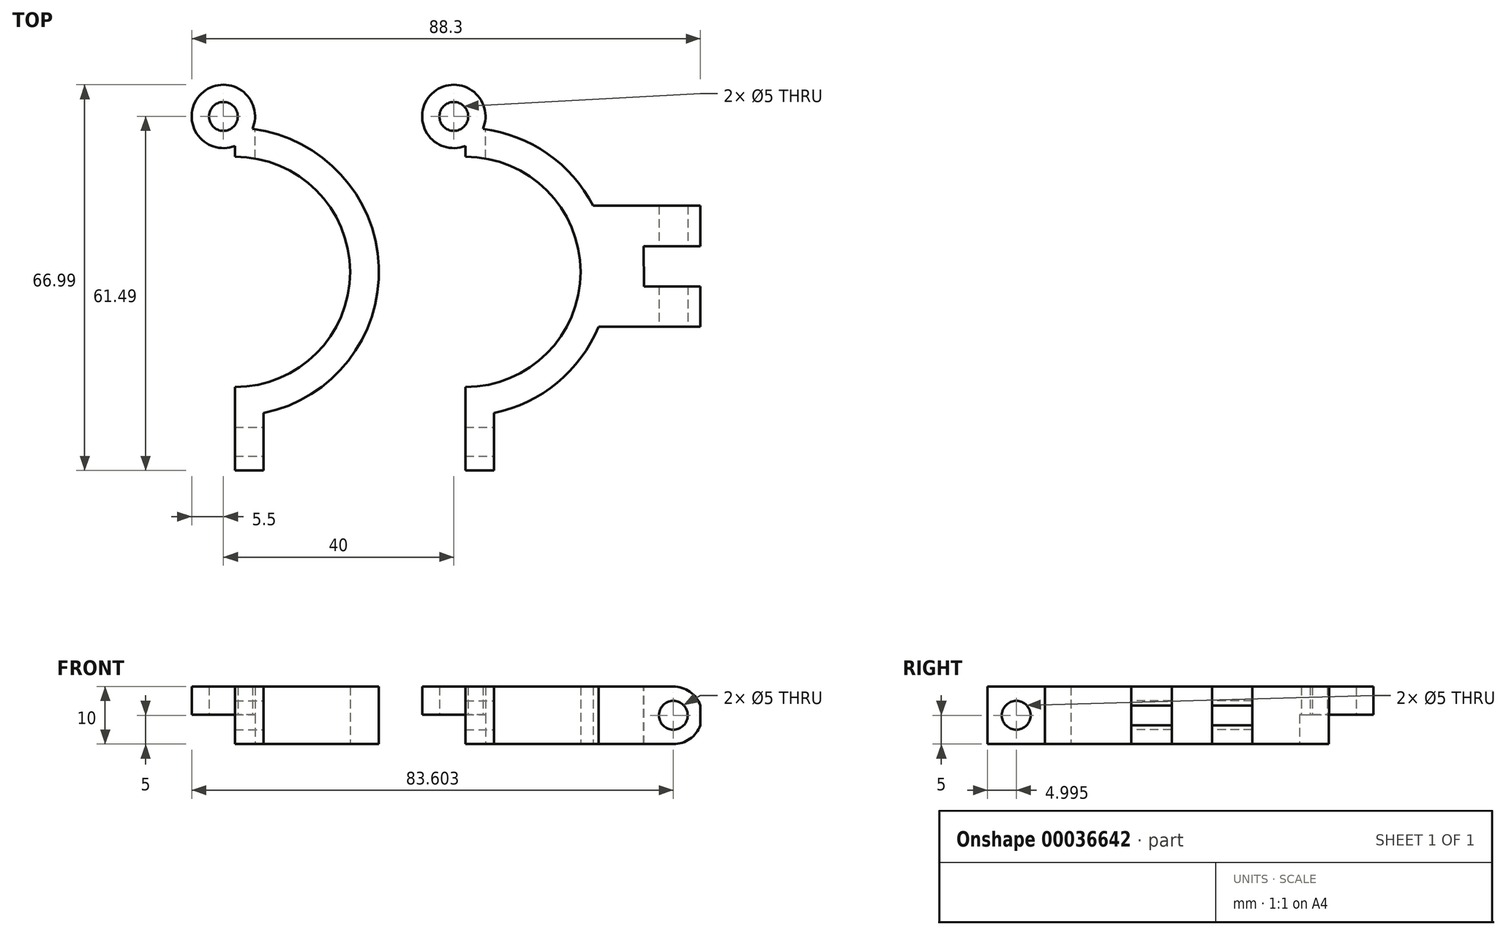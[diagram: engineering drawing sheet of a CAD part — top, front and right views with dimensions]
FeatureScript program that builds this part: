
annotation { "Feature Type Name" : "Feature", "Feature Type Description" : "" }
export const myFeature = defineFeature(function(context is Context, id is Id, definition is map)
    precondition{}
    {
        {
            var Q0;
            Q0=qCreatedBy(makeId("Top.planeOp"),FACE);
            var sketch = newSketch(context, id + "F0", { "sketchPlane" : qUnion([Q0])});
            skArc(sketch, "E0", {"start": v(0, -20) * mm, "mid": v(20, 0) * mm, "end": v(0, 20) * mm});
            skArc(sketch, "E1", {"start": v(5, -24.5) * mm, "mid": v(24.87, 2.51) * mm, "end": v(0, 25) * mm});
            skLineSegment(sketch, "E2", {"start": v(0, 25) * mm, "end": v(0, 20) * mm});
            skLineSegment(sketch, "E3.trimOffspring", {"start": v(0, -20) * mm, "end": v(0, -25) * mm});
            skLineSegment(sketch, "E4.top", {"start": v(0, -34.5) * mm, "end": v(5, -34.5) * mm});
            skLineSegment(sketch, "E4.left", {"start": v(0, -20) * mm, "end": v(0, -34.5) * mm});
            skLineSegment(sketch, "E4.right", {"start": v(5, -24.5) * mm, "end": v(5, -34.5) * mm});
            skLineSegment(sketch, "E5", {"start": v(0, 25) * mm, "end": v(-2, 25) * mm, "construction": true});
            skLineSegment(sketch, "E6", {"start": v(-2, 25) * mm, "end": v(-2, 27) * mm, "construction": true});
            skCircle(sketch, "E7", {"center": v(-2, 27) * mm, "radius": 2.5 * mm});
            skCircle(sketch, "E8", {"center": v(-2, 27) * mm, "radius": 5.5 * mm});
            skSolve(sketch);
        }
        {
            var Q0;
            Q0 = qSketchRegion(id + "F0", true);
            extrude(context, id + "F1", {"entities" : qUnion([Q0]), "depth" : 10 * mm});
        }
        {
            var Q0;
            Q0=makeQuery(id+"F1.opExtrude","CAP_FACE",FACE,{"disambiguationData":[OSD([sQuery(id+"F0.wireOp",EDGE,"E0"),sQuery(id+"F0.wireOp",EDGE,"E1"),sQuery(id+"F0.wireOp",EDGE,"E2"),sQuery(id+"F0.wireOp",EDGE,"E4.top"),sQuery(id+"F0.wireOp",EDGE,"E4.left"),sQuery(id+"F0.wireOp",EDGE,"E4.right"),sQuery(id+"F0.wireOp",EDGE,"40993b52-42f4-45ce-a234-201135d0f319"),sQuery(id+"F0.wireOp",EDGE,"b42522cb-95ce-463a-b71a-0f81370b394c")])],"isStart":true});
            var sketch = newSketch(context, id + "F2", { "sketchPlane" : qUnion([Q0])});
            skArc(sketch, "E9.0", {"start": v(3.5, -27) * mm, "mid": v(-6.54, -30.1) * mm, "end": v(0, -21.88) * mm});
            skLineSegment(sketch, "E10.bottom", {"start": v(0, -15.05) * mm, "end": v(3.5, -15.05) * mm});
            skLineSegment(sketch, "E10.left", {"start": v(0, -15.05) * mm, "end": v(0, -21.88) * mm});
            skLineSegment(sketch, "E10.right", {"start": v(3.5, -15.05) * mm, "end": v(3.5, -27) * mm});
            skSolve(sketch);
        }
        {
            var Q0;
            Q0 = qSketchRegion(id + "F2", true);
            extrude(context, id + "F3", {"entities" : qUnion([Q0]), "operationType" : NewBodyOperationType.REMOVE, "oppositeDirection" : true, "depth" : 5.1 * mm});
        }
        {
            var Q0;
            Q0=makeQuery(id+"F1.opExtrude","SWEPT_FACE",FACE,{"disambiguationData":[OSD([sQuery(id+"F0.wireOp",EDGE,"E4.right")])]});
            var sketch = newSketch(context, id + "F4", { "sketchPlane" : qUnion([Q0])});
            skLineSegment(sketch, "E11.0.0", {"start": v(-34.5, 0) * mm, "end": v(-24.5, 0) * mm, "construction": true});
            skLineSegment(sketch, "E11.0.1", {"start": v(-24.5, 0) * mm, "end": v(-24.5, 10) * mm, "construction": true});
            skLineSegment(sketch, "E11.0.2", {"start": v(-24.5, 10) * mm, "end": v(-34.5, 10) * mm, "construction": true});
            skLineSegment(sketch, "E11.0.3", {"start": v(-34.5, 10) * mm, "end": v(-34.5, 0) * mm, "construction": true});
            skCircle(sketch, "E12", {"center": v(-29.5, 5) * mm, "radius": 2.5 * mm});
            skPoint(sketch, "E12.centerSnap0", {"position": v(-29.5, 10) * mm});
            skPoint(sketch, "E12.centerSnap1", {"position": v(-34.5, 5) * mm});
            skSolve(sketch);
        }
        {
            var Q0;
            Q0 = qSketchRegion(id + "F4", true);
            extrude(context, id + "F5", {"entities" : qUnion([Q0]), "operationType" : NewBodyOperationType.REMOVE, "oppositeDirection" : true, "depth" : 25 * mm});
        }
        {
            var Q0;
            Q0=makeQuery(id+"F1.opExtrude","SWEPT_BODY",BODY,{"disambiguationData":[OSD([sQuery(id+"F0.wireOp",EDGE,"E0"),sQuery(id+"F0.wireOp",EDGE,"E1"),sQuery(id+"F0.wireOp",EDGE,"E2"),sQuery(id+"F0.wireOp",EDGE,"E4.top"),sQuery(id+"F0.wireOp",EDGE,"E4.left"),sQuery(id+"F0.wireOp",EDGE,"E4.right"),sQuery(id+"F0.wireOp",EDGE,"E7"),sQuery(id+"F0.wireOp",EDGE,"E8")])]});
            transform(context, id + "F6", {"entities" : qUnion([Q0]), "transformType" : TransformType.TRANSLATION_3D, "dx" : 40 * mm, "dy" : 0 * mm, "dz" : 0 * mm, "makeCopy" : true});
        }
        {
            var Q0;
            Q0=makeQuery(id+"F6.opPattern","COPY",FACE,{"derivedFrom":makeQuery(id+"F1.opExtrude","CAP_FACE",FACE,{"disambiguationData":[OSD([sQuery(id+"F0.wireOp",EDGE,"E0"),sQuery(id+"F0.wireOp",EDGE,"E1"),sQuery(id+"F0.wireOp",EDGE,"E2"),sQuery(id+"F0.wireOp",EDGE,"E4.top"),sQuery(id+"F0.wireOp",EDGE,"E4.left"),sQuery(id+"F0.wireOp",EDGE,"E4.right"),sQuery(id+"F0.wireOp",EDGE,"E7"),sQuery(id+"F0.wireOp",EDGE,"E8")])],"isStart":false}),"instanceName":"1"});
            var sketch = newSketch(context, id + "F7", { "sketchPlane" : qUnion([Q0])});
            skLineSegment(sketch, "E13.rect.bottom", {"start": v(61.08, -9.51) * mm, "end": v(81.1, -9.51) * mm});
            skLineSegment(sketch, "E13.rect.top", {"start": v(60.88, 11.49) * mm, "end": v(80.89, 11.49) * mm});
            skPoint(sketch, "E13.rect.middle", {"position": v(64.98, 0.99) * mm});
            skLineSegment(sketch, "E14.0", {"start": v(61.08, -9.51) * mm, "end": v(60.88, 11.49) * mm});
            skLineSegment(sketch, "E15.0", {"start": v(60.88, 4.49) * mm, "end": v(60.95, 4.49) * mm});
            skLineSegment(sketch, "E16.0", {"start": v(60.88, -2.51) * mm, "end": v(61.01, -2.51) * mm});
            skLineSegment(sketch, "E17.0", {"start": v(71.08, -9.6) * mm, "end": v(71.08, -9.51) * mm});
            skLineSegment(sketch, "E18.trimOffspring", {"start": v(70.95, 4.49) * mm, "end": v(80.89, 4.49) * mm});
            skLineSegment(sketch, "E19.trimOffspring", {"start": v(71.01, -2.51) * mm, "end": v(81.01, -2.51) * mm});
            skLineSegment(sketch, "E20.trimOffspring", {"start": v(71.01, -2.51) * mm, "end": v(70.95, 4.49) * mm});
            skLineSegment(sketch, "E21", {"start": v(80.89, 11.49) * mm, "end": v(80.89, 4.49) * mm});
            skLineSegment(sketch, "E22", {"start": v(81.01, -2.51) * mm, "end": v(81.1, -9.51) * mm});
            skSolve(sketch);
        }
        {
            var Q0;
            Q0 = qSketchRegion(id + "F7", true);
            extrude(context, id + "F8", {"entities" : qUnion([Q0]), "operationType" : NewBodyOperationType.ADD, "oppositeDirection" : true, "depth" : 10 * mm});
        }
        {
            var Q0;
            Q0=makeQuery(id+"F8.opExtrude","SWEPT_FACE",FACE,{"disambiguationData":[OSD([sQuery(id+"F7.wireOp",EDGE,"E13.rect.bottom")])]});
            var sketch = newSketch(context, id + "F9", { "sketchPlane" : qUnion([Q0])});
            skLineSegment(sketch, "E23.0", {"start": v(71.1, 0) * mm, "end": v(71.1, 10) * mm});
            skLineSegment(sketch, "E24.0.1", {"start": v(71.1, 0) * mm, "end": v(81.1, 0) * mm});
            skLineSegment(sketch, "E24.0.2", {"start": v(81.1, 0) * mm, "end": v(81.1, 10) * mm});
            skLineSegment(sketch, "E24.0.3", {"start": v(81.1, 10) * mm, "end": v(71.1, 10) * mm});
            skCircle(sketch, "E25", {"center": v(76.1, 5) * mm, "radius": 2.5 * mm});
            skPoint(sketch, "E25.centerSnap0", {"position": v(81.1, 5) * mm});
            skPoint(sketch, "E25.centerSnap1", {"position": v(76.1, 10) * mm});
            skSolve(sketch);
        }
        {
            var Q0;
            Q0=makeQuery(id+"F9.imprint","IMPRINT",FACE,{"disambiguationData":[TD([[makeQuery(id+"F9.imprint","IMPRINT",EDGE,{"derivedFrom":sQuery(id+"F9.wireOp",EDGE,"E25")}),1.0]])]});
            extrude(context, id + "F10", {"entities" : qUnion([Q0]), "operationType" : NewBodyOperationType.REMOVE, "oppositeDirection" : true, "depth" : 25 * mm});
        }
        {
            var Q0;
            Q0=makeQuery(id+"F8.opExtrude","SWEPT_FACE",FACE,{"disambiguationData":[OSD([sQuery(id+"F7.wireOp",EDGE,"E13.rect.bottom")])]});
            var sketch = newSketch(context, id + "F11", { "sketchPlane" : qUnion([Q0])});
            skArc(sketch, "E26", {"start": v(76.1, 0) * mm, "mid": v(81.1, 5) * mm, "end": v(76.1, 10) * mm});
            skLineSegment(sketch, "E27.bottom", {"start": v(81.1, 10) * mm, "end": v(76.1, 10) * mm});
            skLineSegment(sketch, "E27.top", {"start": v(80.98, 0) * mm, "end": v(76.1, 0) * mm});
            skLineSegment(sketch, "E28.0", {"start": v(80.8, 0) * mm, "end": v(80.8, 10) * mm});
            skSolve(sketch);
        }
        {
            var Q0;
            {var subQ3=sQuery(id+"F11.wireOp",EDGE,"E27.bottom");Q0=makeQuery(id+"F11.imprint","IMPRINT",FACE,{"disambiguationData":[TD([[makeQuery(id+"F11.imprint","IMPRINT",EDGE,{"derivedFrom":subQ3}),-1.0]])]});}
            var Q1;
            {var subQ3=sQuery(id+"F11.wireOp",EDGE,"E27.top");Q1=makeQuery(id+"F11.imprint","IMPRINT",FACE,{"disambiguationData":[TD([[makeQuery(id+"F11.imprint","IMPRINT",EDGE,{"derivedFrom":subQ3}),1.0]])]});}
            var Q2;
            {var subQ3=sQuery(id+"F11.wireOp",EDGE,"E27.top");var subQ5=sQuery(id+"F11.wireOp",EDGE,"E28.0");var subQ7=makeQuery(id+"F11.imprint","INTERSECT",VERTEX,{"derivedFrom":[subQ3,subQ5]});Q2=makeQuery(id+"F11.imprint","IMPRINT",FACE,{"disambiguationData":[TD([[makeQuery(id+"F11.imprint","IMPRINT",EDGE,{"disambiguationData":[TD([[subQ7,-1.0]])],"derivedFrom":subQ5}),-1.0]])]});}
            var Q3;
            {var subQ3=sQuery(id+"F11.wireOp",EDGE,"E27.bottom");var subQ5=sQuery(id+"F11.wireOp",EDGE,"E28.0");var subQ7=makeQuery(id+"F11.imprint","INTERSECT",VERTEX,{"derivedFrom":[subQ3,subQ5]});Q3=makeQuery(id+"F11.imprint","IMPRINT",FACE,{"disambiguationData":[TD([[makeQuery(id+"F11.imprint","IMPRINT",EDGE,{"disambiguationData":[TD([[subQ7,1.0]])],"derivedFrom":subQ5}),-1.0]])]});}
            var Q4;
            {var subQ0=sQuery(id+"F11.wireOp",EDGE,"E28.0");var subQ1=sQuery(id+"F11.wireOp",EDGE,"E26");var subQ3=makeQuery(id+"F11.imprint","INTERSECT",VERTEX,{"disambiguationData":[OD(0.0)],"derivedFrom":[subQ1,subQ0]});Q4=makeQuery(id+"F11.imprint","IMPRINT",FACE,{"disambiguationData":[TD([[makeQuery(id+"F11.imprint","IMPRINT",EDGE,{"disambiguationData":[TD([[subQ3,-1.0]])],"derivedFrom":subQ0}),-1.0]])]});}
            extrude(context, id + "F12", {"entities" : qUnion([Q0, Q1, Q2, Q3, Q4]), "operationType" : NewBodyOperationType.REMOVE, "oppositeDirection" : true, "depth" : 25 * mm});
        }
    });
